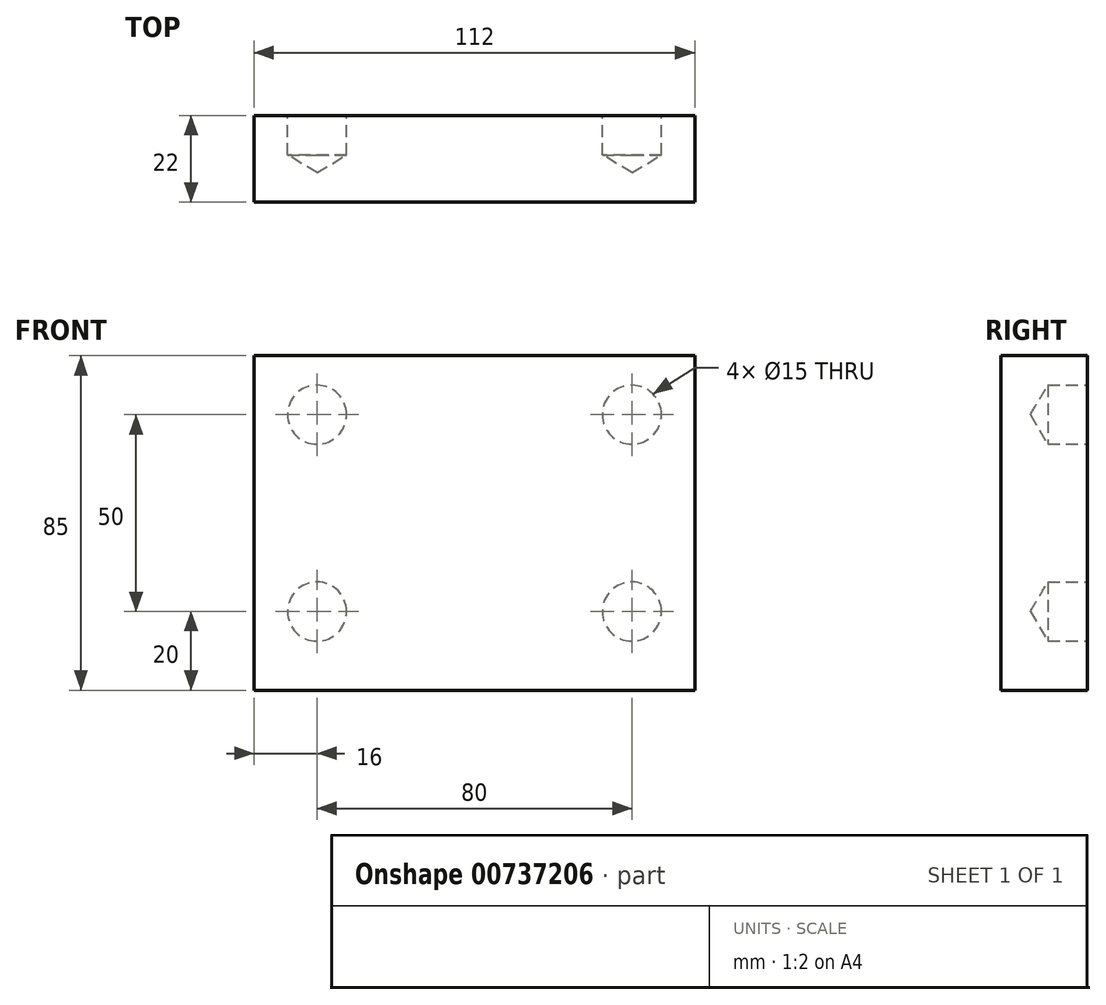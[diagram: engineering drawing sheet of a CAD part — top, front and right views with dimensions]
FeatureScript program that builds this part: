
annotation { "Feature Type Name" : "Feature", "Feature Type Description" : "" }
export const myFeature = defineFeature(function(context is Context, id is Id, definition is map)
    precondition{}
    {
        {
            var Q0;
            Q0=qCreatedBy(makeId("Top.planeOp"),FACE);
            var sketch = newSketch(context, id + "F0", { "sketchPlane" : qUnion([Q0])});
            skLineSegment(sketch, "E0", {"start": v(-56, 11) * mm, "end": v(56, 11) * mm});
            skLineSegment(sketch, "E1", {"start": v(56, 11) * mm, "end": v(56, -11) * mm});
            skLineSegment(sketch, "E2", {"start": v(56, -11) * mm, "end": v(-56, -11) * mm});
            skLineSegment(sketch, "E3", {"start": v(-56, -11) * mm, "end": v(-56, 11) * mm});
            skSolve(sketch);
        }
        {
            var Q0;
            Q0=makeQuery(id+"F0.imprint","IMPRINT",FACE,{"disambiguationData":[TD([[makeQuery(id+"F0.imprint","IMPRINT",EDGE,{"derivedFrom":sQuery(id+"F0.wireOp",EDGE,"E0")}),-1.0]])]});
            extrude(context, id + "F1", {"entities" : qUnion([Q0]), "oppositeDirection" : true, "depth" : 85 * mm, "offsetDistance" : 25 * mm});
        }
        {
            var Q0;
            Q0=makeQuery(id+"F1.opExtrude","SWEPT_FACE",FACE,{"disambiguationData":[OSD([sQuery(id+"F0.wireOp",EDGE,"E2")])]});
            var sketch = newSketch(context, id + "F2", { "sketchPlane" : qUnion([Q0])});
            skPoint(sketch, "E4", {"position": v(-40, -15) * mm});
            skPoint(sketch, "E5", {"position": v(0, -40) * mm});
            skPoint(sketch, "E6", {"position": v(40, -15) * mm});
            skPoint(sketch, "E7", {"position": v(40, -65) * mm});
            skPoint(sketch, "E8", {"position": v(-40, -65) * mm});
            skLineSegment(sketch, "E9", {"start": v(-44.74, -40) * mm, "end": v(51.82, -40) * mm, "construction": true});
            skSolve(sketch);
        }
        {
            var Q0;
            Q0=makeQuery(id+"F1.opExtrude","SWEPT_FACE",FACE,{"disambiguationData":[OSD([sQuery(id+"F0.wireOp",EDGE,"E0")])]});
            var sketch = newSketch(context, id + "F3", { "sketchPlane" : qUnion([Q0])});
            skPoint(sketch, "E10.0", {"position": v(-40, -15) * mm});
            skPoint(sketch, "E11.0", {"position": v(0, -40) * mm});
            skPoint(sketch, "E12.0", {"position": v(40, -15) * mm});
            skPoint(sketch, "E13.0", {"position": v(40, -65) * mm});
            skPoint(sketch, "E14.0", {"position": v(-40, -65) * mm});
            skSolve(sketch);
        }
        {
            var Q0;
            Q0=sQuery(id+"F3.wireOp",VERTEX,"E10.0");
            var Q1;
            Q1=sQuery(id+"F3.wireOp",VERTEX,"E12.0");
            var Q2;
            Q2=sQuery(id+"F3.wireOp",VERTEX,"E13.0");
            var Q3;
            Q3=sQuery(id+"F3.wireOp",VERTEX,"E14.0");
            var Q4;
            Q4=makeQuery(id+"F1.opExtrude","SWEPT_BODY",BODY,{"disambiguationData":[OSD([sQuery(id+"F0.wireOp",EDGE,"E0"),sQuery(id+"F0.wireOp",EDGE,"E1"),sQuery(id+"F0.wireOp",EDGE,"E2"),sQuery(id+"F0.wireOp",EDGE,"E3")])]});
            hole(context, id + "F4", {"style" : HoleStyle.SIMPLE, "endStyle" : HoleEndStyle.BLIND, "holeDiameter" : 15 * mm, "majorDiameter" : 3 * mm, "holeDepth" : 10 * mm, "isTappedThrough" : true, "tappedDepth" : 12 * mm, "tapClearance" : 3, "locations" : qUnion([Q0, Q1, Q2, Q3]), "scope" : qUnion([Q4])});
        }
    });
